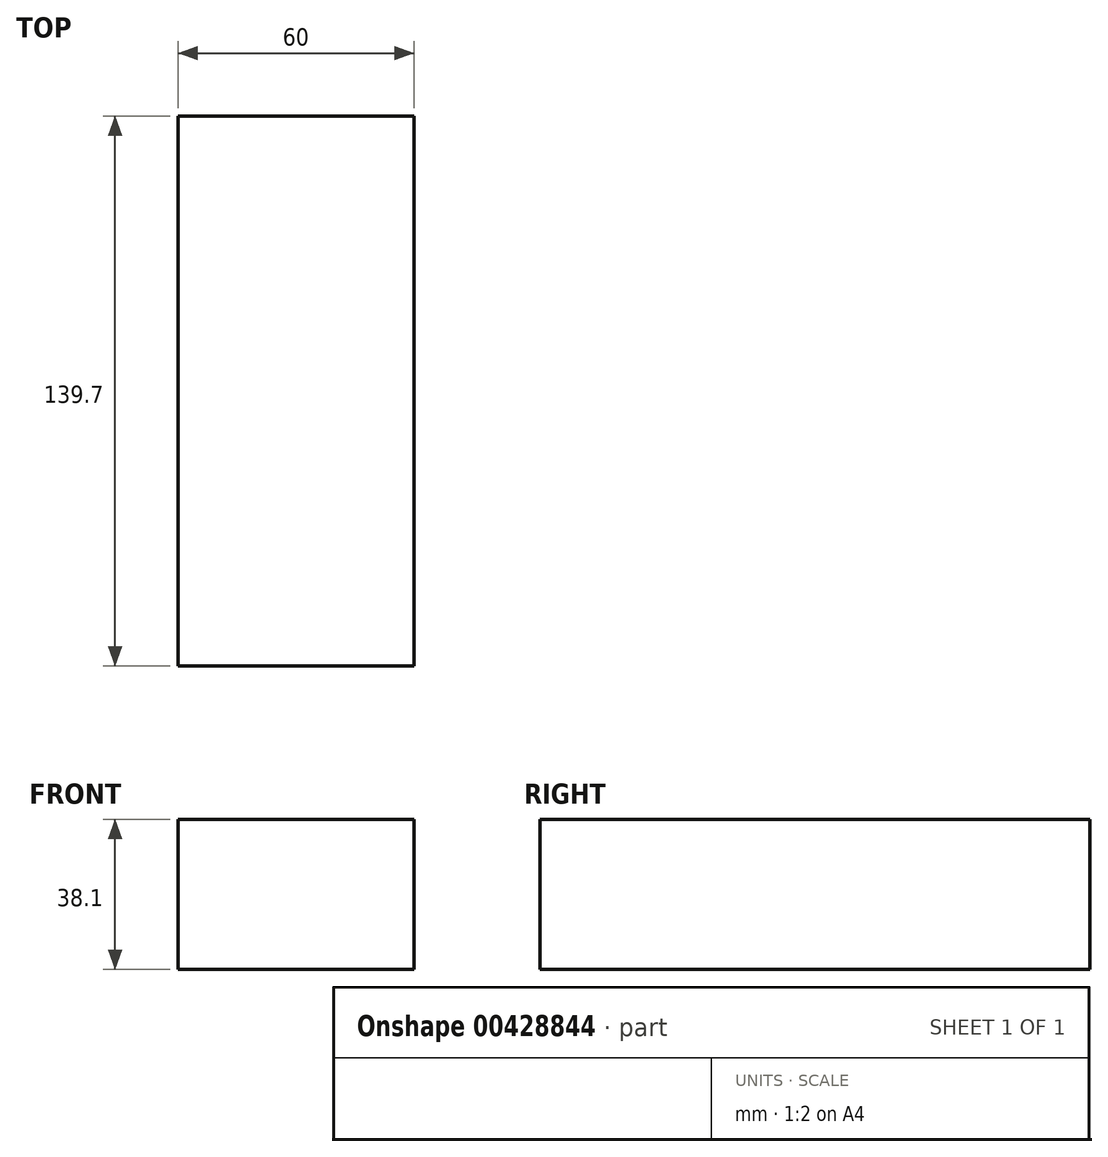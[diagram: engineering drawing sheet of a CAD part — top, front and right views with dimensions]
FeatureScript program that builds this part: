
annotation { "Feature Type Name" : "Feature", "Feature Type Description" : "" }
export const myFeature = defineFeature(function(context is Context, id is Id, definition is map)
    precondition{}
    {
        {
            assignVariable(context, id + "F0", {"name" : "Length", "anyValue" : 60});
        }
        {
            var Q0;
            Q0=qCreatedBy(makeId("Right.planeOp"),FACE);
            var sketch = newSketch(context, id + "F1", { "sketchPlane" : qUnion([Q0])});
            skLineSegment(sketch, "E0.bottom", {"start": v(69.85, -19.05) * mm, "end": v(-69.85, -19.05) * mm});
            skLineSegment(sketch, "E0.top", {"start": v(69.85, 19.05) * mm, "end": v(-69.85, 19.05) * mm});
            skLineSegment(sketch, "E0.left", {"start": v(69.85, -19.05) * mm, "end": v(69.85, 19.05) * mm});
            skLineSegment(sketch, "E0.right", {"start": v(-69.85, -19.05) * mm, "end": v(-69.85, 19.05) * mm});
            skPoint(sketch, "E0.middle", {"position": v(0, 0) * mm});
            skSolve(sketch);
        }
        {
            var Q0;
            Q0 = qSketchRegion(id + "F1", true);
            extrude(context, id + "F2", {"entities" : qUnion([Q0]), "depth" : (getVariable(context, 'Length')) * mm, "symmetric" : true});
        }
    });
